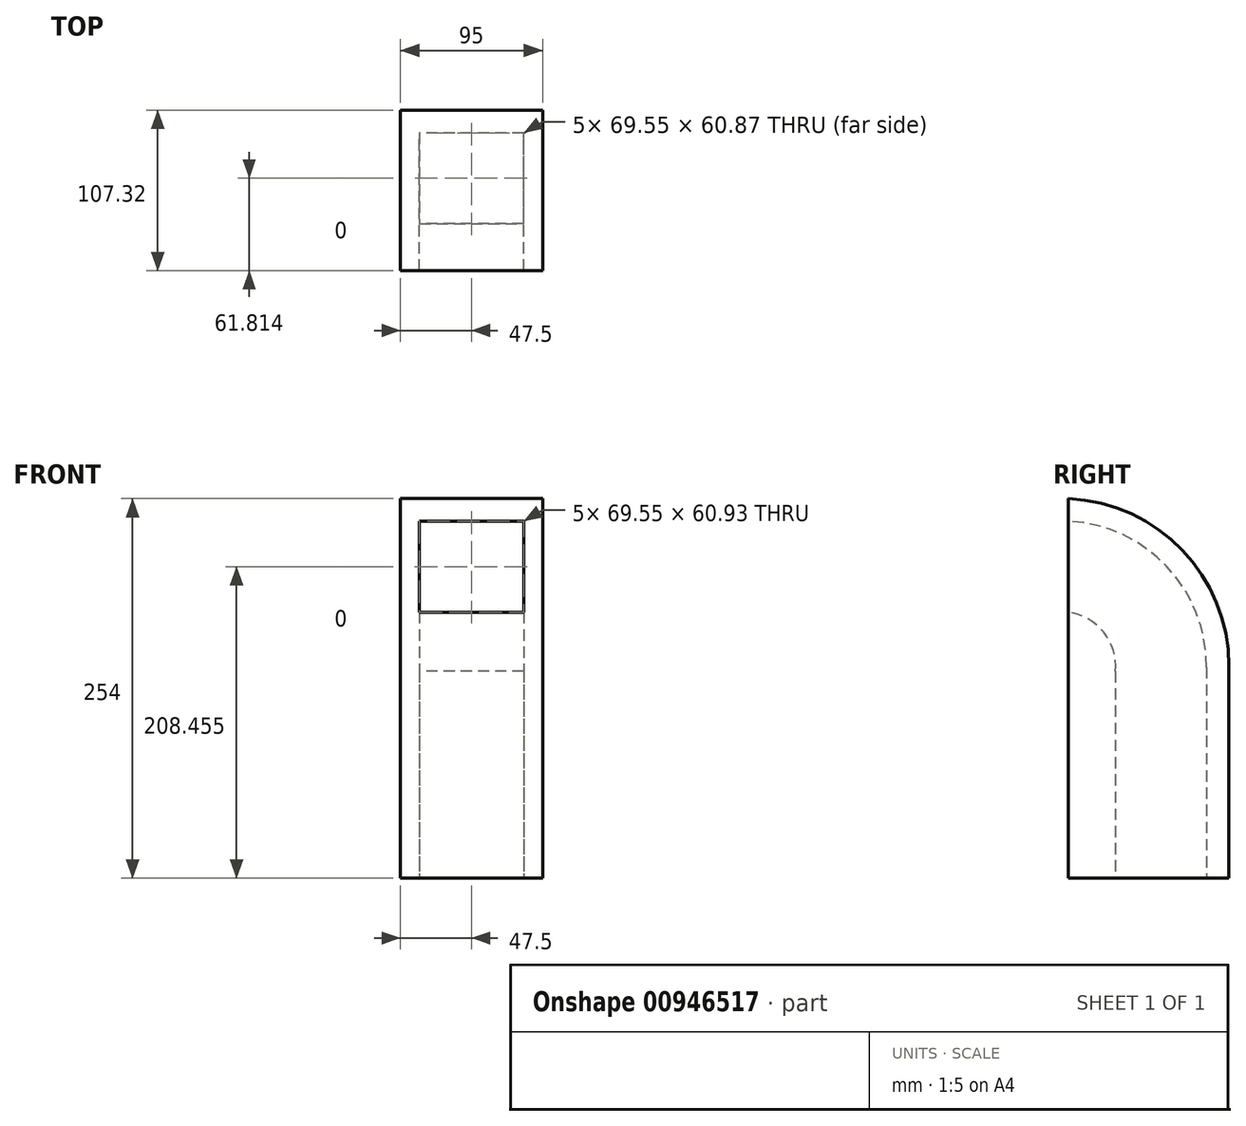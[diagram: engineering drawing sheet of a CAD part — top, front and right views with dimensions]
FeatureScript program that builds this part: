
annotation { "Feature Type Name" : "Feature", "Feature Type Description" : "" }
export const myFeature = defineFeature(function(context is Context, id is Id, definition is map)
    precondition{}
    {
        {
            var Q0;
            Q0=qCreatedBy(makeId("Top.planeOp"),FACE);
            var sketch = newSketch(context, id + "F0", { "sketchPlane" : qUnion([Q0])});
            skLineSegment(sketch, "E0.bottom", {"start": v(47.5, 53.66) * mm, "end": v(-47.5, 53.66) * mm});
            skLineSegment(sketch, "E0.top", {"start": v(47.5, -53.66) * mm, "end": v(-47.5, -53.66) * mm});
            skLineSegment(sketch, "E0.left", {"start": v(47.5, 53.66) * mm, "end": v(47.5, -53.66) * mm});
            skLineSegment(sketch, "E0.right", {"start": v(-47.5, 53.66) * mm, "end": v(-47.5, -53.66) * mm});
            skPoint(sketch, "E0.middle", {"position": v(0, 0) * mm});
            skSolve(sketch);
        }
        {
            var Q0;
            Q0=makeQuery(id+"F0.imprint","IMPRINT",FACE,{"disambiguationData":[TD([[makeQuery(id+"F0.imprint","IMPRINT",EDGE,{"derivedFrom":sQuery(id+"F0.wireOp",EDGE,"E0.bottom")}),1.0]])]});
            extrude(context, id + "F1", {"entities" : qUnion([Q0]), "depth" : 254 * mm, "offsetDistance" : 25.4 * mm});
        }
        {
            var Q0;
            Q0=makeQuery(id+"F1.opExtrude","CAP_EDGE",EDGE,{"disambiguationData":[OSD([sQuery(id+"F0.wireOp",EDGE,"E0.bottom")])],"isStart":false});
            fillet(context, id + "F2", {"entities" : qUnion([Q0]), "radius" : 112.22 * mm, "tangentPropagation" : true, "allowEdgeOverflow" : false});
        }
        {
            var Q0;
            Q0=makeQuery(id+"F1.opExtrude","SWEPT_FACE",FACE,{"disambiguationData":[OSD([sQuery(id+"F0.wireOp",EDGE,"E0.top")])]});
            var sketch = newSketch(context, id + "F3", { "sketchPlane" : qUnion([Q0])});
            skLineSegment(sketch, "E1.bottom", {"start": v(34.77, 238.92) * mm, "end": v(-34.77, 238.92) * mm});
            skLineSegment(sketch, "E1.top", {"start": v(34.77, 178) * mm, "end": v(-34.77, 178) * mm});
            skLineSegment(sketch, "E1.left", {"start": v(34.77, 238.92) * mm, "end": v(34.77, 178) * mm});
            skLineSegment(sketch, "E1.right", {"start": v(-34.77, 238.92) * mm, "end": v(-34.77, 178) * mm});
            skPoint(sketch, "E1.middle", {"position": v(0, 208.45) * mm});
            skPoint(sketch, "E1.middle.positionSnap0", {"position": v(0, 254) * mm});
            skPoint(sketch, "E1.centerSnap0", {"position": v(0, 254) * mm});
            skSolve(sketch);
        }
        {
            var Q0;
            Q0=makeQuery(id+"F3.imprint","IMPRINT",FACE,{"disambiguationData":[TD([[makeQuery(id+"F3.imprint","IMPRINT",EDGE,{"derivedFrom":sQuery(id+"F3.wireOp",EDGE,"E1.bottom")}),1.0]])]});
            var Q1;
            Q1=makeQuery(id+"F2.opFillet","BLEND_EDGE",EDGE,{"blendedFrom":[makeQuery(id+"F1.opExtrude","CAP_EDGE",EDGE,{"disambiguationData":[OSD([sQuery(id+"F0.wireOp",EDGE,"E0.bottom")])],"isStart":false}),makeQuery(id+"F1.opExtrude","SWEPT_FACE",FACE,{"disambiguationData":[OSD([sQuery(id+"F0.wireOp",EDGE,"E0.right")])]})],"blendedInto":[makeQuery(id+"F1.opExtrude","SWEPT_FACE",FACE,{"disambiguationData":[OSD([sQuery(id+"F0.wireOp",EDGE,"E0.right")])]})]});
            var Q2;
            Q2=makeQuery(id+"F1.opExtrude","SWEPT_EDGE",EDGE,{"disambiguationData":[OSD([sQuery(id+"F0.wireOp",EDGE,"E0.bottom"),sQuery(id+"F0.wireOp",EDGE,"E0.right")])]});
            sweep(context, id + "F4", {"operationType" : NewBodyOperationType.REMOVE, "profiles" : qUnion([Q0]), "path" : qUnion([Q1, Q2])});
        }
    });
